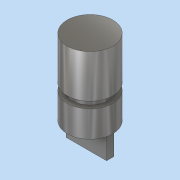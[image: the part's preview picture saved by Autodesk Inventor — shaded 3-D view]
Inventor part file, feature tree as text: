
AUTODESK INVENTOR PART (.ipt)
format: ipt  version: 2019.4 (Build 234330000, 330)  size: 115,200 bytes
history: native  units: mm
features: sketch x2, revolve x1, extrude x1, projected_geometry x1
ambient origin geometry x8: Origin, YZ Plane, XZ Plane, XY Plane, X Axis, Y Axis, Z Axis, Center Point
bodies: Solid1 (feature_tree)
feature tree (5):
  revolve  "Revolution1"  [1 undecoded]
  extrude  "Extrusion1"  Depth=0.86mm
  sketch  "Sketch1"  dims[d1=3.0mm d2=5.66mm]
  sketch  "Sketch2"  dims[d4=90.0deg d6=0.86mm d8=10.0mm d9=2.41mm d10=3.0mm d11=0.0mm]
  projected_geometry  "Projected Loop1"
note: 1 required parameter value undecoded (feature->parameter linkage not recoverable at this tier; creation-order binding heuristic only, values carry confidence <= 0.55)
